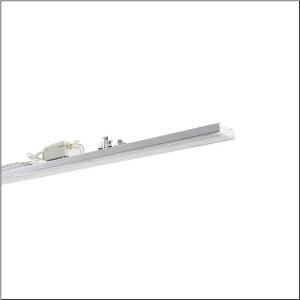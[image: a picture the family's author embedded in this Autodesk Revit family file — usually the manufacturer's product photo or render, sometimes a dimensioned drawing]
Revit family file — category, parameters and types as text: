
# Revit family: licross_r__21_recessed_mo_52te18dn495g_fa09
name_source: partatom
category: Lighting Fixtures
units: mm (PartAtom-declared; Revit-internal decimal feet)

## family parameters
Cut with Voids When Loaded = No
Host = Face
Light Source = No
Part Type = Normal
Room Calculation Point = No
Round Connector Dimension = Use Diameter
Shared = No

## types (1)
- --- (1 x LED, 9990 lm, 58 W, 4000K)
    Apparent Load = 58 VA
    CIE Flux Codes = 79 95 99 100 100
    Color Rendering = 80
    Color Temperature = 4000K
    Default Elevation = 1800 mm
    Description = Licross® 21 Recessed MO, luminaire insert, of sheet steel, galvanised, coil coated, white, length: 1.500mm, width: 66mm, height: 67mm, LED rated luminous flux: 9.990lm, light colour: 840, control gear: DALI 2, with plug, 5-pole, with phase selection, mains connection: 220..240V, AC, 50/60Hz, rated input power: 58W, halogen-free wiring, primary light control with lens, of plastic, primary optical cover: cover, of PMMA, light emission: direct distribution, primary light characteristic: symmetric, protection rating (complete): IP54, insulation class (complete): insulation class I (protective earthing), certification: CE, ENEC, VDE, UKCA, protection symbol: D if used in an environment with non-conductive dust loads with corresponding accessories, impact resistance: IK06, permissible ambient temperature for indoor applications: -25..+35°C, corresponds to IFS (International Featured Standards) requirements for safety and quality in the food industry, reducing of maximum allowable ambient temperature of 5°C with ceiling mounting, LABS conformity tested according to VDMA 24364:2018-05, packaging unit: 1 piece
    Height = 58 mm
    Lamp = 1 x LED
    Lamp Light Flux = 9990 lm
    Lamp Power = 58 W
    Lamp count = 1
    Length = 1500 mm
    Luminous efficacy = 172 lm/W
    Manufacturer = Siteco
    ModVariant = No
    Model = 52TE18DN495G
    Mounting Place = Ceiling
    Mounting Type = Pendant
    Number of Poles = 1
    OnlyDefault = Yes
    Power Factor = 1
    Product Name = Licross® 21 Recessed MO
    Product group = luminaire insert
    ProductGroupID = 901
    Protection Class = Protection class I
    Protection Degree = IP 54
    RLX_Detail_Level = 1
    RLX_Emergency_Light_Flux = 0 lm
    RLX_Emergency_Type = 0
    RLX_Emergency_Type_DB = No
    RlxData = <blob elided: 24469 chars, md5=20e6be43>
    Socket = socket
    Standby Power = 0 W
    System Light Flux = 9990 lm
    System Power = 58 W
    Type Comments = factory setting: luminous flux: 100 % | dim-lin: 254 | 390 mA
    Type Image = l_1296930.jpg
    URL = http://relux.com
    VarID = @adj_057459
    Voltage = 0 V
    Weight = 0.00 kg
    Width = 66 mm

## geometry (parser evidence)
native form markers: Blend x4, Sweep x11
no freeform markers — native parametric forms only
